# Revit family: Panel de interconexión
name_source: partatom
category: Equipement spécialisé
units: mm (PartAtom-declared; Revit-internal decimal feet)

## family parameters
Basée sur le plan de construction = Non
Cote de connecteur circulaire = Utiliser le diamètre
Couper avec des vides une fois chargée = Non
Partagée = Oui
Point de calcul de pièce = Non
Toujours verticalement = Oui
Type d'élément = Normal

## types (1)
- Panel de interconexión
    Altura = 43.8 mm  [stored 0.143701 ft]
    Anchura (mm) = 482.6 mm
    Blindado = Oui
    Clasificación ETIM = EC001128
    Color = IDS_NOIR
    E-catalogo enlace = https://www.legrand.fr
    EAN = 3414972185509
    Elévation par défaut = 0 mm  [stored 0 ft]
    Formulación BIM = Panel de interconexión a equipar con 24 RJ45 Cat 5e 6 6A Keystone con anillo portador metal
    Función = Paneles de interconexión conectores cobre
    IK = IK04
    Módulos de altura = 1
    Natura del cable para la conexión = Flexible
    Numero RAL = 9017
    Número de conectores = 24
    Número de pieza Legrand = 632850
    Profundidad = 140 mm  [stored 0.459318 ft]
    Tamaño modular = 19 pulgadas
    Temperatura de almacenamiento = -10_à_70
    Temperatura operativa = -10_à_60
    Tipo de conector = RJ45

note: [stored X ft] marks values corroborated as IEEE doubles in the binary element streams (Revit-internal decimal feet)
